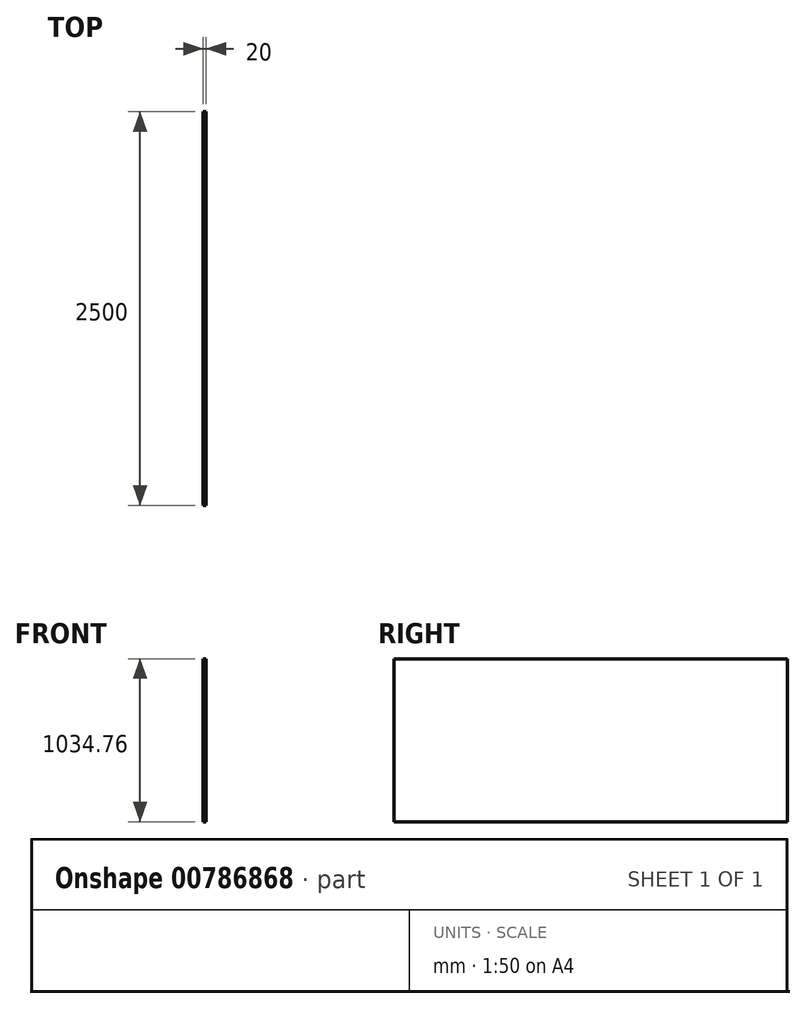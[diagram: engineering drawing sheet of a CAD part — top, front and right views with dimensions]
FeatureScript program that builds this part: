
annotation { "Feature Type Name" : "Feature", "Feature Type Description" : "" }
export const myFeature = defineFeature(function(context is Context, id is Id, definition is map)
    precondition{}
    {
        {
            var Q0;
            Q0=qCreatedBy(makeId("Top.planeOp"),FACE);
            var sketch = newSketch(context, id + "F0", { "sketchPlane" : qUnion([Q0])});
            skLineSegment(sketch, "E0.bottom", {"start": v(0, 0) * mm, "end": v(20, 0) * mm});
            skLineSegment(sketch, "E0.top", {"start": v(0, -2500) * mm, "end": v(20, -2500) * mm});
            skLineSegment(sketch, "E0.left", {"start": v(0, 0) * mm, "end": v(0, -2500) * mm});
            skLineSegment(sketch, "E0.right", {"start": v(20, 0) * mm, "end": v(20, -2500) * mm});
            skSolve(sketch);
        }
        {
            var Q0;
            Q0=makeQuery(id+"F0.imprint","IMPRINT",FACE,{"disambiguationData":[TD([[makeQuery(id+"F0.imprint","IMPRINT",EDGE,{"derivedFrom":sQuery(id+"F0.wireOp",EDGE,"E0.bottom")}),-1.0]])]});
            extrude(context, id + "F1", {"entities" : qUnion([Q0]), "depth" : 1034.76 * mm, "offsetDistance" : 25 * mm});
        }
    });
